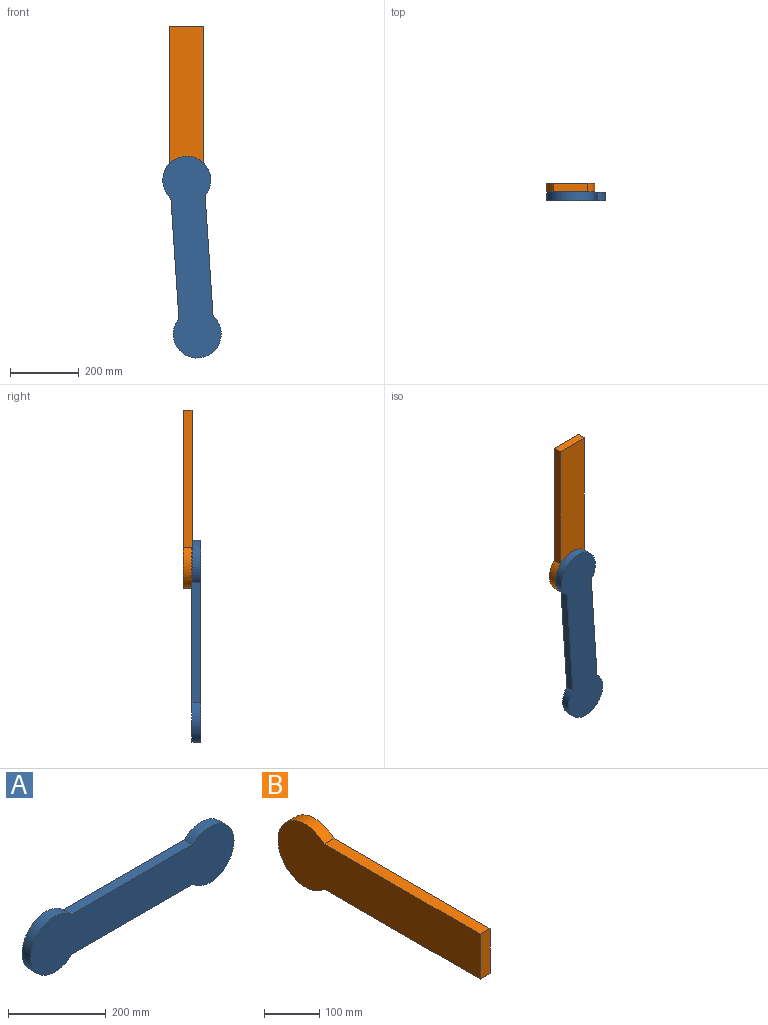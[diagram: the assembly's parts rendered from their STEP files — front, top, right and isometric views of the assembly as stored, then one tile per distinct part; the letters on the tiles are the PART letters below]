
ASSEMBLY  parts=2 mates=2
PART A: 6 faces, bbox 590x25x140 mm
  f0: cylinder r=70mm len=140mm, axis (0,1,0), area 8211mm2, adj f1,f3,f4,f5
  f1: plane 352.02x25mm, normal (0,0,1), area 8800.5mm2, adj f0,f2,f4,f5
  f2: cylinder r=70mm len=140mm, axis (0,1,0), area 8211mm2, adj f1,f3,f4,f5
  f3: plane 352.02x25mm, normal (0,0,-1), area 8800.5mm2, adj f0,f2,f4,f5
  f4: plane 590x140mm, normal (0,-1,0), area 63091.7mm2, adj f0,f1,f2,f3
  f5: plane 590x140mm, normal (0,1,0), area 63091.7mm2, adj f0,f1,f2,f3
PART B: 6 faces, bbox 25x520x140 mm
  f0: cylinder r=70mm len=140mm, axis (-1,0,0), area 8211mm2, adj f1,f3,f4,f5
  f1: plane 401.01x25mm, normal (0,0,1), area 10025.3mm2, adj f0,f2,f4,f5
  f2: plane 100x25mm, normal (0,-1,0), area 2500mm2, adj f1,f3,f4,f5
  f3: plane 401.01x25mm, normal (0,0,-1), area 10025.3mm2, adj f0,f2,f4,f5
  f4: plane 520x140mm, normal (1,0,0), area 54045.9mm2, adj f0,f1,f2,f3
  f5: plane 520x140mm, normal (-1,0,0), area 54045.9mm2, adj f0,f1,f2,f3
PLACE A rot(axis=(0,1,0),86.2deg) t=(-33.28,-44.41,-505.91)mm
PLACE B rot(axis=(-0.58,0.58,-0.58),120deg) t=(-63.34,-31.91,-56.92)mm fixed
MATE revolute B.f0 <-> A.f2  axis (0,-1,0) through (-63.34,-44.41,-56.92)mm
MATE parallel B.f0 <-> A.f2  axis (0,-1,0) through (-63.34,-44.41,-56.92)mm
